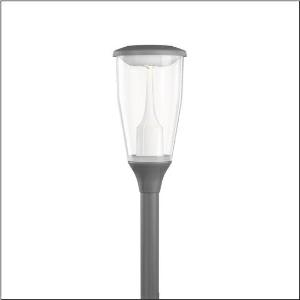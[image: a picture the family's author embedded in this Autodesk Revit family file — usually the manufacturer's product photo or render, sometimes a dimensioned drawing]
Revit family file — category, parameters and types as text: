
# Revit family: dl_11_iq___p1_0a_5xa5575lf14h000022_ea02
name_source: partatom
category: Lighting Fixtures
units: mm (PartAtom-declared; Revit-internal decimal feet)

## family parameters
Cut with Voids When Loaded = No
Host = Face
Light Source = No
Part Type = Normal
Room Calculation Point = No
Round Connector Dimension = Use Diameter
Shared = No

## types (1)
- --- (1 x LED, 1530 lm, 10 W, 4000K)
    Apparent Load = 10 VA
    CIE Flux Codes = 34 63 91 95 100
    Color Rendering = 70
    Color Temperature = 4000K
    Default Elevation = 1800 mm
    Description = DL 11 iQ, mast luminaire, Module 540 iQ-SR, primary light control with 3 zone facetted reflector, of plastic, silver coated, highly specular, structured, primary optical cover: cover, of PMMA, transparent, light distribution: P1.0a, light emission: direct distribution, primary light characteristic: asymmetric, installation type: post-top, LED, High Power LED, light colour: 740, colour temperature: 4000K, control: Street-Remote, Auto-Match, Temp-Guard, Lumen-Switch, Night-Set, Smart-Wire, Light-Fading, Desk-Remote (wireless, voltage-free reading and setting of iQ features in the workshop via application-optimized NFC function/RFID function), optimised constant luminous flux control (CLO 2.0), mains connection: 220..240V, AC, 50/60Hz, connection cable pre-assembled, cable length: 5,5m, start of lifetime: 10W, end of service life: 10W, luminaire housing, upper part, of diecast aluminium, coated, Siteco® metallic grey (DB 702S), spigot size: 76mm (post-top), post-top mast mounting element, of diecast aluminium, coated, Siteco® metallic grey (DB 702S), Module 540 iQ-SR, traffic white (RAL 9016), equipment: standard, protection rating (complete): IP66, insulation class (complete): insulation class II (safety insulation), certification: CE, ENEC, ENEC+, VDE, packaging unit: 1 piece

Light Distribution: P1.0a
    Height = 665 mm
    Lamp = 1 x LED
    Lamp Light Flux = 1530 lm
    Lamp Power = 10 W
    Lamp count = 1
    Length = 334 mm
    Luminous efficacy = 153 lm/W
    Manufacturer = Siteco
    ModVariant = No
    Model = 5XA5575LF14H000022
    Number of Poles = 1
    OnlyDefault = Yes
    Power Factor = 1
    Product Name = DL 11 iQ | P1.0a
    Product group = mast luminaire | pylon top
    ProductGroupID = 6100
    Protection Class = Protection class II
    Protection Degree = IP 66
    RLX_Detail_Level = 1
    RLX_Emergency_Light_Flux = 0 lm
    RLX_Emergency_Type = 0
    RLX_Emergency_Type_DB = No
    RlxData = <blob elided: 108913 chars, md5=0a407865>
    Socket = socket
    Standby Power = 0 W
    System Light Flux = 1530 lm
    System Power = 10 W
    Type Comments = factory setting: luminous flux: 100 % | dim-lin: 254 | 401 mA
    Type Image = l_1258354.jpg
    URL = http://relux.com
    VarID = @adj_060503
    Voltage = 0 V
    Weight = 0.00 kg
    Width = 0 mm  [stored 0 ft]

note: [stored X ft] marks values corroborated as IEEE doubles in the binary element streams (Revit-internal decimal feet)

## geometry (parser evidence)
native form markers: Blend x4, Sweep x9
no freeform markers — native parametric forms only
